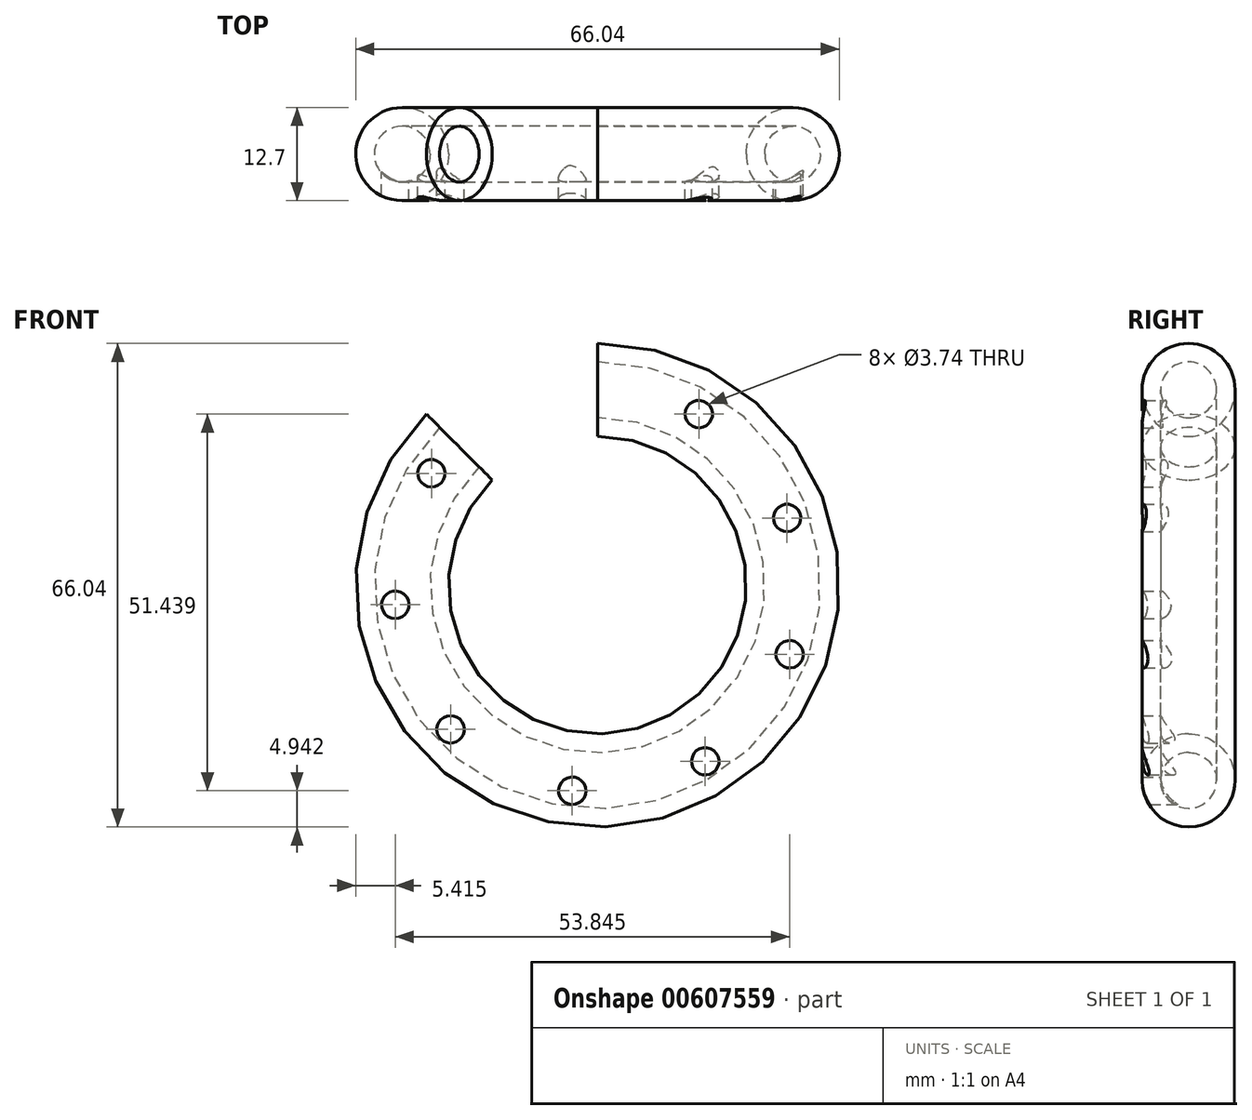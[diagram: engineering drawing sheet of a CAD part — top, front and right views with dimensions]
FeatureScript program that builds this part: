
annotation { "Feature Type Name" : "Feature", "Feature Type Description" : "" }
export const myFeature = defineFeature(function(context is Context, id is Id, definition is map)
    precondition{}
    {
        {
            var Q0;
            Q0=qCreatedBy(makeId("Right.planeOp"),FACE);
            var sketch = newSketch(context, id + "F0", { "sketchPlane" : qUnion([Q0])});
            skCircle(sketch, "E0", {"center": v(0, 0) * mm, "radius": 6.35 * mm});
            skLineSegment(sketch, "E1", {"start": v(-62.9, -26.67) * mm, "end": v(153.13, -26.67) * mm});
            skSolve(sketch);
        }
        {
            var Q0;
            Q0=makeQuery(id+"F0.imprint","IMPRINT",FACE,{"disambiguationData":[TD([[makeQuery(id+"F0.imprint","IMPRINT",EDGE,{"derivedFrom":sQuery(id+"F0.wireOp",EDGE,"E0")}),1.0]])]});
            var Q1;
            Q1=sQuery(id+"F0.wireOp",EDGE,"E1");
            revolve(context, id + "F1", {"entities" : qUnion([Q0]), "axis" : qUnion([Q1]), "revolveType" : RevolveType.ONE_DIRECTION, "angle" : 315 * degree});
        }
        {
            var Q0;
            Q0=makeQuery(id+"F1.opRevolve","CAP_FACE",FACE,{"disambiguationData":[OSD([sQuery(id+"F0.wireOp",EDGE,"E0")])],"isStart":false});
            var Q1;
            Q1=makeQuery(id+"F1.opRevolve","CAP_FACE",FACE,{"disambiguationData":[OSD([sQuery(id+"F0.wireOp",EDGE,"E0")])],"isStart":true});
            shell(context, id + "F2", {"entities" : qUnion([Q0, Q1]), "thickness" : 2.54 * mm});
        }
        {
            var Q0;
            Q0=qCreatedBy(makeId("Front.planeOp"),FACE);
            var sketch = newSketch(context, id + "F3", { "sketchPlane" : qUnion([Q0])});
            skCircle(sketch, "E2", {"center": v(13.85, -3.3) * mm, "radius": 1.87 * mm});
            skCircle(sketch, "E3.1.0", {"center": v(25.9, -17.5) * mm, "radius": 1.87 * mm});
            skCircle(sketch, "E3.2.0", {"center": v(26.24, -36.1) * mm, "radius": 1.87 * mm});
            skCircle(sketch, "E3.3.0", {"center": v(14.72, -50.72) * mm, "radius": 1.87 * mm});
            skCircle(sketch, "E3.4.0", {"center": v(-3.45, -54.75) * mm, "radius": 1.87 * mm});
            skCircle(sketch, "E3.5.0", {"center": v(-20.06, -46.36) * mm, "radius": 1.87 * mm});
            skCircle(sketch, "E3.6.0", {"center": v(-27.6, -29.35) * mm, "radius": 1.87 * mm});
            skCircle(sketch, "E3.7.0", {"center": v(-22.67, -11.4) * mm, "radius": 1.87 * mm});
            skPoint(sketch, "E3.center", {"position": v(0, -27.28) * mm});
            skLineSegment(sketch, "E3.anchor1", {"start": v(0, -27.28) * mm, "end": v(13.85, -3.3) * mm, "construction": true});
            skLineSegment(sketch, "E3.anchor2", {"start": v(0, -27.28) * mm, "end": v(-22.67, -11.4) * mm, "construction": true});
            skSolve(sketch);
        }
        {
            var Q0;
            Q0 = qSketchRegion(id + "F3", true);
            extrude(context, id + "F4", {"entities" : qUnion([Q0]), "operationType" : NewBodyOperationType.REMOVE, "endBound" : BoundingType.THROUGH_ALL, "depth" : 25.4 * mm, "offsetDistance" : 25.4 * mm});
        }
    });
